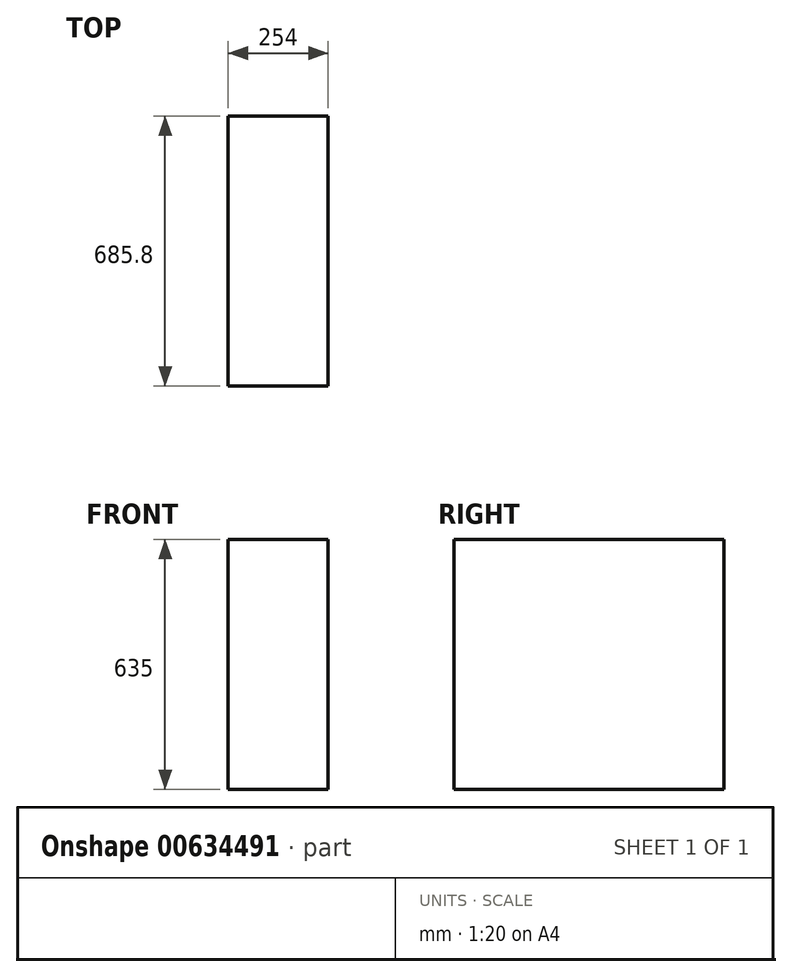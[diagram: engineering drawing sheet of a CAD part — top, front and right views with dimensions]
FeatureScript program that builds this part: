
annotation { "Feature Type Name" : "Feature", "Feature Type Description" : "" }
export const myFeature = defineFeature(function(context is Context, id is Id, definition is map)
    precondition{}
    {
        {
            var Q0;
            Q0=qCreatedBy(makeId("Top.planeOp"),FACE);
            var sketch = newSketch(context, id + "F0", { "sketchPlane" : qUnion([Q0])});
            skLineSegment(sketch, "E0.bottom", {"start": v(0, 0) * mm, "end": v(254, 0) * mm});
            skLineSegment(sketch, "E0.top", {"start": v(0, -685.8) * mm, "end": v(254, -685.8) * mm});
            skLineSegment(sketch, "E0.left", {"start": v(0, 0) * mm, "end": v(0, -685.8) * mm});
            skLineSegment(sketch, "E0.right", {"start": v(254, 0) * mm, "end": v(254, -685.8) * mm});
            skSolve(sketch);
        }
        {
            var Q0;
            Q0=makeQuery(id+"F0.imprint","IMPRINT",FACE,{"disambiguationData":[TD([[makeQuery(id+"F0.imprint","IMPRINT",EDGE,{"derivedFrom":sQuery(id+"F0.wireOp",EDGE,"E0.bottom")}),-1.0]])]});
            extrude(context, id + "F1", {"entities" : qUnion([Q0]), "depth" : 635 * mm});
        }
    });
